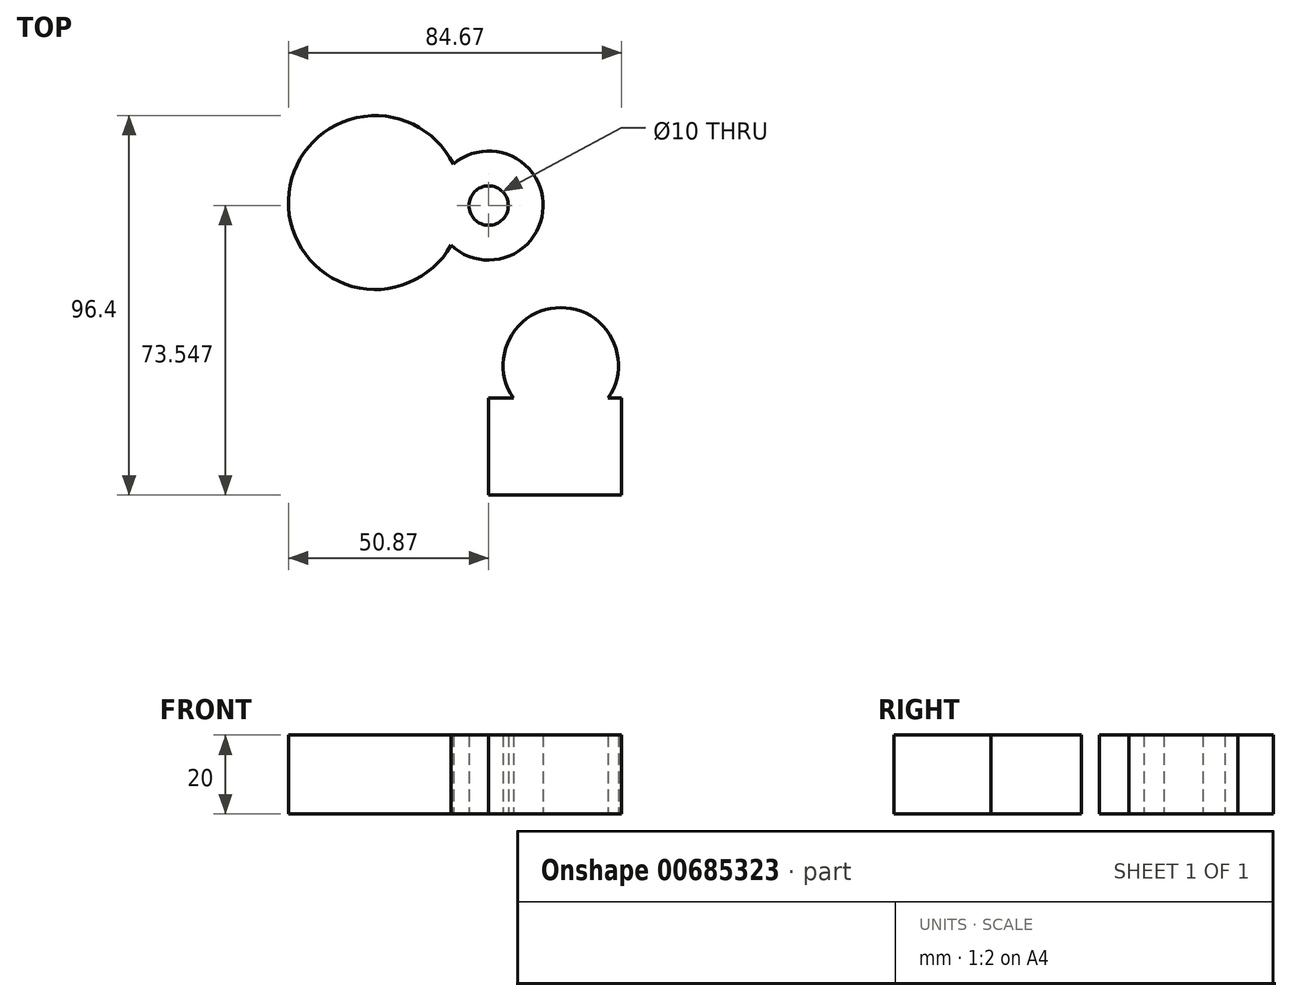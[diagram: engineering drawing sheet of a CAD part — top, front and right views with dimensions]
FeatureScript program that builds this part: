
annotation { "Feature Type Name" : "Feature", "Feature Type Description" : "" }
export const myFeature = defineFeature(function(context is Context, id is Id, definition is map)
    precondition{}
    {
        {
            var Q0;
            Q0=qCreatedBy(makeId("Top.planeOp"),FACE);
            var sketch = newSketch(context, id + "F0", { "sketchPlane" : qUnion([Q0])});
            skLineSegment(sketch, "E0.bottom", {"start": v(0, -16.85) * mm, "end": v(33.8, -16.85) * mm});
            skLineSegment(sketch, "E0.top", {"start": v(0, -41.45) * mm, "end": v(33.8, -41.45) * mm});
            skLineSegment(sketch, "E0.left", {"start": v(0, -16.85) * mm, "end": v(0, -41.45) * mm});
            skLineSegment(sketch, "E0.right", {"start": v(33.8, -16.85) * mm, "end": v(33.8, -41.45) * mm});
            skSolve(sketch);
        }
        {
            var Q0;
            Q0=makeQuery(id+"F0.imprint","IMPRINT",FACE,{"disambiguationData":[TD([[makeQuery(id+"F0.imprint","IMPRINT",EDGE,{"derivedFrom":sQuery(id+"F0.wireOp",EDGE,"E0.bottom")}),-1.0]])]});
            extrude(context, id + "F1", {"entities" : qUnion([Q0]), "depth" : 20 * mm, "offsetDistance" : 25 * mm});
        }
        {
            var Q0;
            Q0=qCreatedBy(makeId("Top.planeOp"),FACE);
            var sketch = newSketch(context, id + "F2", { "sketchPlane" : qUnion([Q0])});
            skCircle(sketch, "E1", {"center": v(0, 32.1) * mm, "radius": 13.85 * mm});
            skSolve(sketch);
        }
        {
            var Q0;
            Q0 = qSketchRegion(id + "F2", true);
            extrude(context, id + "F3", {"entities" : qUnion([Q0]), "depth" : 20 * mm, "offsetDistance" : 25 * mm});
        }
        {
            var Q0;
            Q0=qCreatedBy(makeId("Top.planeOp"),FACE);
            var sketch = newSketch(context, id + "F4", { "sketchPlane" : qUnion([Q0])});
            skCircle(sketch, "E2", {"center": v(18.33, -8.49) * mm, "radius": 14.66 * mm});
            skSolve(sketch);
        }
        {
            var Q0;
            Q0 = qSketchRegion(id + "F4", true);
            extrude(context, id + "F5", {"entities" : qUnion([Q0]), "operationType" : NewBodyOperationType.ADD, "depth" : 20 * mm, "offsetDistance" : 25 * mm});
        }
        {
            var Q0;
            Q0=sQuery(id+"F2.wireOp",VERTEX,"E1.center");
            var Q1;
            Q1=makeQuery(id+"F3.opExtrude","SWEPT_BODY",BODY,{"disambiguationData":[OSD([sQuery(id+"F2.wireOp",EDGE,"E1")])]});
            hole(context, id + "F6", {"style" : HoleStyle.SIMPLE, "endStyle" : HoleEndStyle.THROUGH, "oppositeDirection" : true, "holeDiameter" : 10 * mm, "majorDiameter" : 5 * mm, "isTappedThrough" : true, "tappedDepth" : 12 * mm, "tapClearance" : 3, "locations" : qUnion([Q0]), "scope" : qUnion([Q1])});
        }
        {
            var Q0;
            Q0=qCreatedBy(makeId("Top.planeOp"),FACE);
            var sketch = newSketch(context, id + "F7", { "sketchPlane" : qUnion([Q0])});
            skCircle(sketch, "E3", {"center": v(-28.78, 32.87) * mm, "radius": 22.09 * mm});
            skSolve(sketch);
        }
        {
            var Q0;
            Q0 = qSketchRegion(id + "F7", true);
            extrude(context, id + "F8", {"entities" : qUnion([Q0]), "operationType" : NewBodyOperationType.ADD, "depth" : 20 * mm, "offsetDistance" : 25 * mm});
        }
    });
